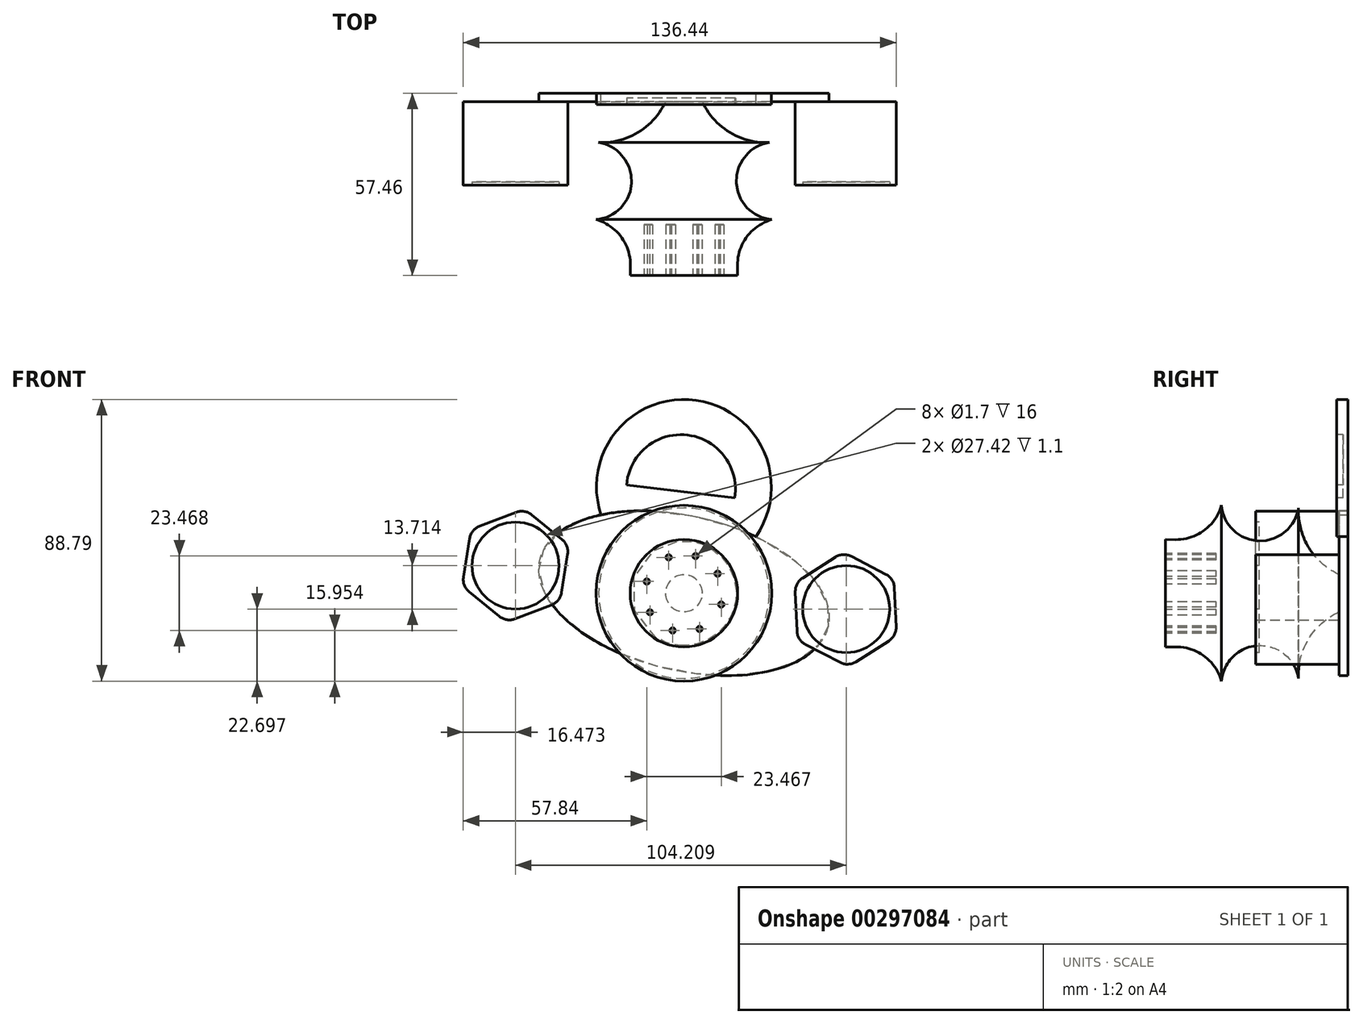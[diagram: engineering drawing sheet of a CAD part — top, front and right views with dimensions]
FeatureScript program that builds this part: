
annotation { "Feature Type Name" : "Feature", "Feature Type Description" : "" }
export const myFeature = defineFeature(function(context is Context, id is Id, definition is map)
    precondition{}
    {
        {
            var Q0;
            Q0=qCreatedBy(makeId("Top.planeOp"),FACE);
            var sketch = newSketch(context, id + "F0", { "sketchPlane" : qUnion([Q0])});
            skLineSegment(sketch, "E0", {"start": v(0, 0) * mm, "end": v(0, 54.76) * mm});
            skLineSegment(sketch, "E1", {"start": v(0, 54.76) * mm, "end": v(5.83, 54.76) * mm});
            skArc(sketch, "E2", {"start": v(5.83, 54.76) * mm, "mid": v(14.4, 45.15) * mm, "end": v(26.88, 41.91) * mm});
            skArc(sketch, "E3", {"start": v(26.88, 41.91) * mm, "mid": v(16.81, 27.05) * mm, "end": v(32.41, 18.18) * mm});
            skArc(sketch, "E4", {"start": v(32.41, 18.18) * mm, "mid": v(21.41, 14.04) * mm, "end": v(16.89, 3.19) * mm});
            skLineSegment(sketch, "E5", {"start": v(16.89, 3.19) * mm, "end": v(16.93, 0) * mm});
            skLineSegment(sketch, "E6", {"start": v(16.93, 0) * mm, "end": v(0, 0) * mm});
            skSolve(sketch);
        }
        {
            var Q0;
            Q0=makeQuery(id+"F0.imprint","IMPRINT",FACE,{"disambiguationData":[TD([[makeQuery(id+"F0.imprint","IMPRINT",EDGE,{"derivedFrom":sQuery(id+"F0.wireOp",EDGE,"E0")}),-1.0]])]});
            var Q1;
            Q1=sQuery(id+"F0.wireOp",EDGE,"E0");
            revolve(context, id + "F1", {"entities" : qUnion([Q0]), "axis" : qUnion([Q1]), "revolveType" : RevolveType.FULL});
        }
        {
            var Q0;
            Q0=makeQuery(id+"F1.opRevolve","SWEPT_FACE",FACE,{"disambiguationData":[OSD([sQuery(id+"F0.wireOp",EDGE,"E6")])]});
            var sketch = newSketch(context, id + "F2", { "sketchPlane" : qUnion([Q0])});
            skCircle(sketch, "E7", {"center": v(-4.81, 11.3) * mm, "radius": 0.85 * mm});
            skCircle(sketch, "E8", {"center": v(10.62, 6.17) * mm, "radius": 0.85 * mm});
            skCircle(sketch, "E9", {"center": v(11.76, -3.54) * mm, "radius": 0.85 * mm});
            skCircle(sketch, "E10", {"center": v(4.9, -11.26) * mm, "radius": 0.85 * mm});
            skCircle(sketch, "E11", {"center": v(-10.7, -6.01) * mm, "radius": 0.85 * mm});
            skCircle(sketch, "E12", {"center": v(-11.7, 3.7) * mm, "radius": 0.85 * mm});
            skCircle(sketch, "E13", {"center": v(3.66, 11.72) * mm, "radius": 0.85 * mm});
            skCircle(sketch, "E14", {"center": v(-3.58, -11.75) * mm, "radius": 0.85 * mm});
            skSolve(sketch);
        }
        {
            var Q0;
            Q0 = qSketchRegion(id + "F2", true);
            extrude(context, id + "F3", {"entities" : qUnion([Q0]), "operationType" : NewBodyOperationType.REMOVE, "oppositeDirection" : true, "depth" : 16 * mm});
        }
        {
            var Q0;
            Q0=makeQuery(id+"F1.opRevolve","SWEPT_FACE",FACE,{"disambiguationData":[OSD([sQuery(id+"F0.wireOp",EDGE,"E1")])]});
            var sketch = newSketch(context, id + "F4", { "sketchPlane" : qUnion([Q0])});
            skEllipse(sketch, "E15", {"center": v(0, 0) * mm, "majorRadius": 46.6 * mm, "minorRadius": 24.4 * mm, "majorAxis": v(-0.97, -0.22)});
            skSolve(sketch);
        }
        {
            var Q0;
            Q0 = qSketchRegion(id + "F4", true);
            extrude(context, id + "F5", {"entities" : qUnion([Q0]), "depth" : 2.7 * mm});
        }
        {
            var Q0;
            Q0=makeQuery(id+"F5.opExtrude","CAP_FACE",FACE,{"disambiguationData":[OSD([sQuery(id+"F4.wireOp",EDGE,"E15")])],"isStart":true});
            var sketch = newSketch(context, id + "F6", { "sketchPlane" : qUnion([Q0])});
            skCircle(sketch, "E16.cCircle", {"center": v(50.99, -5.1) * mm, "radius": 15.64 * mm, "construction": true});
            skLineSegment(sketch, "E16.0", {"start": v(67, -13.44) * mm, "end": v(51.78, -23.14) * mm});
            skLineSegment(sketch, "E16.1", {"start": v(51.78, -23.14) * mm, "end": v(35.76, -14.8) * mm});
            skLineSegment(sketch, "E16.2", {"start": v(35.76, -14.8) * mm, "end": v(34.97, 3.24) * mm});
            skLineSegment(sketch, "E16.3", {"start": v(34.97, 3.24) * mm, "end": v(50.2, 12.94) * mm});
            skLineSegment(sketch, "E16.4", {"start": v(50.2, 12.94) * mm, "end": v(66.22, 4.6) * mm});
            skLineSegment(sketch, "E16.5", {"start": v(66.22, 4.6) * mm, "end": v(67, -13.44) * mm});
            skPoint(sketch, "E16.0.midPoint", {"position": v(59.4, -18.29) * mm});
            skCircle(sketch, "E17.cCircle", {"center": v(-53.08, 8.71) * mm, "radius": 15.64 * mm, "construction": true});
            skLineSegment(sketch, "E17.0", {"start": v(-39.06, -2.68) * mm, "end": v(-55.93, -9.12) * mm});
            skLineSegment(sketch, "E17.1", {"start": v(-55.93, -9.12) * mm, "end": v(-69.95, 2.27) * mm});
            skLineSegment(sketch, "E17.2", {"start": v(-69.95, 2.27) * mm, "end": v(-67.1, 20.1) * mm});
            skLineSegment(sketch, "E17.3", {"start": v(-67.1, 20.1) * mm, "end": v(-50.22, 26.54) * mm});
            skLineSegment(sketch, "E17.4", {"start": v(-50.22, 26.54) * mm, "end": v(-36.2, 15.15) * mm});
            skLineSegment(sketch, "E17.5", {"start": v(-36.2, 15.15) * mm, "end": v(-39.06, -2.68) * mm});
            skPoint(sketch, "E17.0.midPoint", {"position": v(-47.5, -5.9) * mm});
            skSolve(sketch);
        }
        {
            var Q0;
            Q0 = qSketchRegion(id + "F6", true);
            extrude(context, id + "F7", {"entities" : qUnion([Q0]), "operationType" : NewBodyOperationType.ADD, "depth" : 25 * mm});
        }
        {
            var Q0;
            Q0 = qSketchRegion(id + "F6", true);
            extrude(context, id + "F8", {"entities" : qUnion([Q0]), "operationType" : NewBodyOperationType.ADD, "depth" : 26.3 * mm});
        }
        {
            var Q0;
            Q0 = qSketchRegion(id + "F6", true);
            extrude(context, id + "F9", {"entities" : qUnion([Q0]), "operationType" : NewBodyOperationType.ADD, "depth" : 25 * mm});
        }
        {
            var Q0;
            Q0=makeQuery(id+"F8.opExtrude","CAP_FACE",FACE,{"disambiguationData":[OSD([sQuery(id+"F6.wireOp",EDGE,"E17.0"),sQuery(id+"F6.wireOp",EDGE,"E17.1"),sQuery(id+"F6.wireOp",EDGE,"E17.2"),sQuery(id+"F6.wireOp",EDGE,"E17.3"),sQuery(id+"F6.wireOp",EDGE,"E17.4"),sQuery(id+"F6.wireOp",EDGE,"E17.5")])],"isStart":false});
            var sketch = newSketch(context, id + "F10", { "sketchPlane" : qUnion([Q0])});
            skLineSegment(sketch, "E18", {"start": v(-50.22, 26.54) * mm, "end": v(-55.93, -9.12) * mm});
            skLineSegment(sketch, "E19", {"start": v(-68.52, 11.19) * mm, "end": v(-37.63, 6.24) * mm});
            skCircle(sketch, "E20", {"center": v(-53.08, 8.71) * mm, "radius": 13.7 * mm});
            skCircle(sketch, "E21", {"center": v(51.13, -5) * mm, "radius": 13.7 * mm});
            skSolve(sketch);
        }
        {
            var Q0;
            Q0 = qSketchRegion(id + "F10", true);
            extrude(context, id + "F11", {"entities" : qUnion([Q0]), "operationType" : NewBodyOperationType.REMOVE, "oppositeDirection" : true, "depth" : 1.1 * mm});
        }
        {
            var Q0;
            {var subQ0=sQuery(id+"F6.wireOp",EDGE,"E16.1");var subQ1=sQuery(id+"F6.wireOp",EDGE,"E16.0");Q0=makeQuery(id+"F8.boolean.opBoolean","MERGE",EDGE,{"derivedFrom":[makeQuery(id+"F7.opExtrude","SWEPT_EDGE",EDGE,{"disambiguationData":[OSD([subQ1,subQ0])]}),makeQuery(id+"F8.opExtrude","SWEPT_EDGE",EDGE,{"disambiguationData":[OSD([subQ1,subQ0])]})]});}
            var Q1;
            {var subQ0=sQuery(id+"F6.wireOp",EDGE,"E16.2");var subQ1=sQuery(id+"F6.wireOp",EDGE,"E16.1");Q1=makeQuery(id+"F8.boolean.opBoolean","MERGE",EDGE,{"derivedFrom":[makeQuery(id+"F7.opExtrude","SWEPT_EDGE",EDGE,{"disambiguationData":[OSD([subQ1,subQ0])]}),makeQuery(id+"F8.opExtrude","SWEPT_EDGE",EDGE,{"disambiguationData":[OSD([subQ1,subQ0])]})]});}
            var Q2;
            {var subQ0=sQuery(id+"F6.wireOp",EDGE,"E16.5");var subQ1=sQuery(id+"F6.wireOp",EDGE,"E16.0");Q2=makeQuery(id+"F8.boolean.opBoolean","MERGE",EDGE,{"derivedFrom":[makeQuery(id+"F7.opExtrude","SWEPT_EDGE",EDGE,{"disambiguationData":[OSD([subQ1,subQ0])]}),makeQuery(id+"F8.opExtrude","SWEPT_EDGE",EDGE,{"disambiguationData":[OSD([subQ1,subQ0])]})]});}
            var Q3;
            {var subQ0=sQuery(id+"F6.wireOp",EDGE,"E16.5");var subQ1=sQuery(id+"F6.wireOp",EDGE,"E16.4");Q3=makeQuery(id+"F8.boolean.opBoolean","MERGE",EDGE,{"derivedFrom":[makeQuery(id+"F7.opExtrude","SWEPT_EDGE",EDGE,{"disambiguationData":[OSD([subQ1,subQ0])]}),makeQuery(id+"F8.opExtrude","SWEPT_EDGE",EDGE,{"disambiguationData":[OSD([subQ1,subQ0])]})]});}
            var Q4;
            {var subQ0=sQuery(id+"F6.wireOp",EDGE,"E16.4");var subQ1=sQuery(id+"F6.wireOp",EDGE,"E16.3");Q4=makeQuery(id+"F8.boolean.opBoolean","MERGE",EDGE,{"derivedFrom":[makeQuery(id+"F7.opExtrude","SWEPT_EDGE",EDGE,{"disambiguationData":[OSD([subQ1,subQ0])]}),makeQuery(id+"F8.opExtrude","SWEPT_EDGE",EDGE,{"disambiguationData":[OSD([subQ1,subQ0])]})]});}
            var Q5;
            {var subQ0=sQuery(id+"F6.wireOp",EDGE,"E16.3");var subQ1=sQuery(id+"F6.wireOp",EDGE,"E16.2");Q5=makeQuery(id+"F8.boolean.opBoolean","MERGE",EDGE,{"derivedFrom":[makeQuery(id+"F7.opExtrude","SWEPT_EDGE",EDGE,{"disambiguationData":[OSD([subQ1,subQ0])]}),makeQuery(id+"F8.opExtrude","SWEPT_EDGE",EDGE,{"disambiguationData":[OSD([subQ1,subQ0])]})]});}
            var Q6;
            {var subQ0=sQuery(id+"F6.wireOp",EDGE,"E17.1");var subQ1=sQuery(id+"F6.wireOp",EDGE,"E17.0");Q6=makeQuery(id+"F8.boolean.opBoolean","MERGE",EDGE,{"derivedFrom":[makeQuery(id+"F7.opExtrude","SWEPT_EDGE",EDGE,{"disambiguationData":[OSD([subQ1,subQ0])]}),makeQuery(id+"F8.opExtrude","SWEPT_EDGE",EDGE,{"disambiguationData":[OSD([subQ1,subQ0])]})]});}
            var Q7;
            {var subQ0=sQuery(id+"F6.wireOp",EDGE,"E17.2");var subQ1=sQuery(id+"F6.wireOp",EDGE,"E17.1");Q7=makeQuery(id+"F8.boolean.opBoolean","MERGE",EDGE,{"derivedFrom":[makeQuery(id+"F7.opExtrude","SWEPT_EDGE",EDGE,{"disambiguationData":[OSD([subQ1,subQ0])]}),makeQuery(id+"F8.opExtrude","SWEPT_EDGE",EDGE,{"disambiguationData":[OSD([subQ1,subQ0])]})]});}
            var Q8;
            {var subQ0=sQuery(id+"F6.wireOp",EDGE,"E17.5");var subQ1=sQuery(id+"F6.wireOp",EDGE,"E17.0");Q8=makeQuery(id+"F8.boolean.opBoolean","MERGE",EDGE,{"derivedFrom":[makeQuery(id+"F7.opExtrude","SWEPT_EDGE",EDGE,{"disambiguationData":[OSD([subQ1,subQ0])]}),makeQuery(id+"F8.opExtrude","SWEPT_EDGE",EDGE,{"disambiguationData":[OSD([subQ1,subQ0])]})]});}
            var Q9;
            {var subQ0=sQuery(id+"F6.wireOp",EDGE,"E17.5");var subQ1=sQuery(id+"F6.wireOp",EDGE,"E17.4");Q9=makeQuery(id+"F8.boolean.opBoolean","MERGE",EDGE,{"derivedFrom":[makeQuery(id+"F7.opExtrude","SWEPT_EDGE",EDGE,{"disambiguationData":[OSD([subQ1,subQ0])]}),makeQuery(id+"F8.opExtrude","SWEPT_EDGE",EDGE,{"disambiguationData":[OSD([subQ1,subQ0])]})]});}
            var Q10;
            {var subQ0=sQuery(id+"F6.wireOp",EDGE,"E17.4");var subQ1=sQuery(id+"F6.wireOp",EDGE,"E17.3");Q10=makeQuery(id+"F8.boolean.opBoolean","MERGE",EDGE,{"derivedFrom":[makeQuery(id+"F7.opExtrude","SWEPT_EDGE",EDGE,{"disambiguationData":[OSD([subQ1,subQ0])]}),makeQuery(id+"F8.opExtrude","SWEPT_EDGE",EDGE,{"disambiguationData":[OSD([subQ1,subQ0])]})]});}
            var Q11;
            {var subQ0=sQuery(id+"F6.wireOp",EDGE,"E17.3");var subQ1=sQuery(id+"F6.wireOp",EDGE,"E17.2");Q11=makeQuery(id+"F8.boolean.opBoolean","MERGE",EDGE,{"derivedFrom":[makeQuery(id+"F7.opExtrude","SWEPT_EDGE",EDGE,{"disambiguationData":[OSD([subQ1,subQ0])]}),makeQuery(id+"F8.opExtrude","SWEPT_EDGE",EDGE,{"disambiguationData":[OSD([subQ1,subQ0])]})]});}
            fillet(context, id + "F12", {"entities" : qUnion([Q0, Q1, Q2, Q3, Q4, Q5, Q6, Q7, Q8, Q9, Q10, Q11]), "radius" : 5 * mm, "tangentPropagation" : true, "allowEdgeOverflow" : false});
        }
        {
            var Q0;
            Q0=makeQuery(id+"F5.opExtrude","CAP_FACE",FACE,{"disambiguationData":[OSD([sQuery(id+"F4.wireOp",EDGE,"E15")])],"isStart":false});
            var sketch = newSketch(context, id + "F13", { "sketchPlane" : qUnion([Q0])});
            skCircle(sketch, "E22", {"center": v(0, 33.53) * mm, "radius": 27.56 * mm});
            skSolve(sketch);
        }
        {
            var Q0;
            {var subQ0=sQuery(id+"F13.wireOp",EDGE,"E22");var subQ1=makeQuery(id+"F5.opExtrude","CAP_EDGE",EDGE,{"disambiguationData":[OSD([sQuery(id+"F4.wireOp",EDGE,"E15")])],"isStart":false});var subQ2=makeQuery(id+"F13.imprint","INTERSECT",VERTEX,{"disambiguationData":[OD(0.0)],"derivedFrom":[subQ1,subQ0]});Q0=makeQuery(id+"F13.imprint","IMPRINT",FACE,{"disambiguationData":[TD([[makeQuery(id+"F13.imprint","IMPRINT",EDGE,{"disambiguationData":[TD([[subQ2,-1.0]])],"derivedFrom":subQ0}),1.0]])]});}
            extrude(context, id + "F14", {"entities" : qUnion([Q0]), "oppositeDirection" : true, "depth" : 3.5 * mm});
        }
        {
            var Q0;
            Q0=makeQuery(id+"F14.opExtrude","CAP_FACE",FACE,{"disambiguationData":[OSD([sQuery(id+"F4.wireOp",EDGE,"E15"),sQuery(id+"F13.wireOp",EDGE,"E22")])],"isStart":true});
            var sketch = newSketch(context, id + "F15", { "sketchPlane" : qUnion([Q0])});
            skArc(sketch, "E23", {"start": v(18.07, 34.14) * mm, "mid": v(-1.09, 49.55) * mm, "end": v(-15.98, 30) * mm});
            skLineSegment(sketch, "E24", {"start": v(-15.98, 30) * mm, "end": v(18.07, 34.14) * mm});
            skSolve(sketch);
        }
        {
            var Q0;
            Q0 = qSketchRegion(id + "F15", true);
            extrude(context, id + "F16", {"entities" : qUnion([Q0]), "operationType" : NewBodyOperationType.ADD, "oppositeDirection" : true, "depth" : 6 * mm});
        }
        {
            var Q0;
            Q0=makeQuery(id+"F16.opExtrude","CAP_FACE",FACE,{"disambiguationData":[OSD([sQuery(id+"F15.wireOp",EDGE,"E23"),sQuery(id+"F15.wireOp",EDGE,"E24")])],"isStart":false});
            var sketch = newSketch(context, id + "F17", { "sketchPlane" : qUnion([Q0])});
            skLineSegment(sketch, "E25", {"start": v(15.98, 30) * mm, "end": v(-18.07, 34.14) * mm});
            skArc(sketch, "E26", {"start": v(15.98, 30) * mm, "mid": v(1.12, 49.83) * mm, "end": v(-18.07, 34.14) * mm});
            skSolve(sketch);
        }
        {
            var Q0;
            Q0 = qSketchRegion(id + "F17", true);
            extrude(context, id + "F18", {"entities" : qUnion([Q0]), "operationType" : NewBodyOperationType.REMOVE, "oppositeDirection" : true, "depth" : 4.5 * mm});
        }
    });
